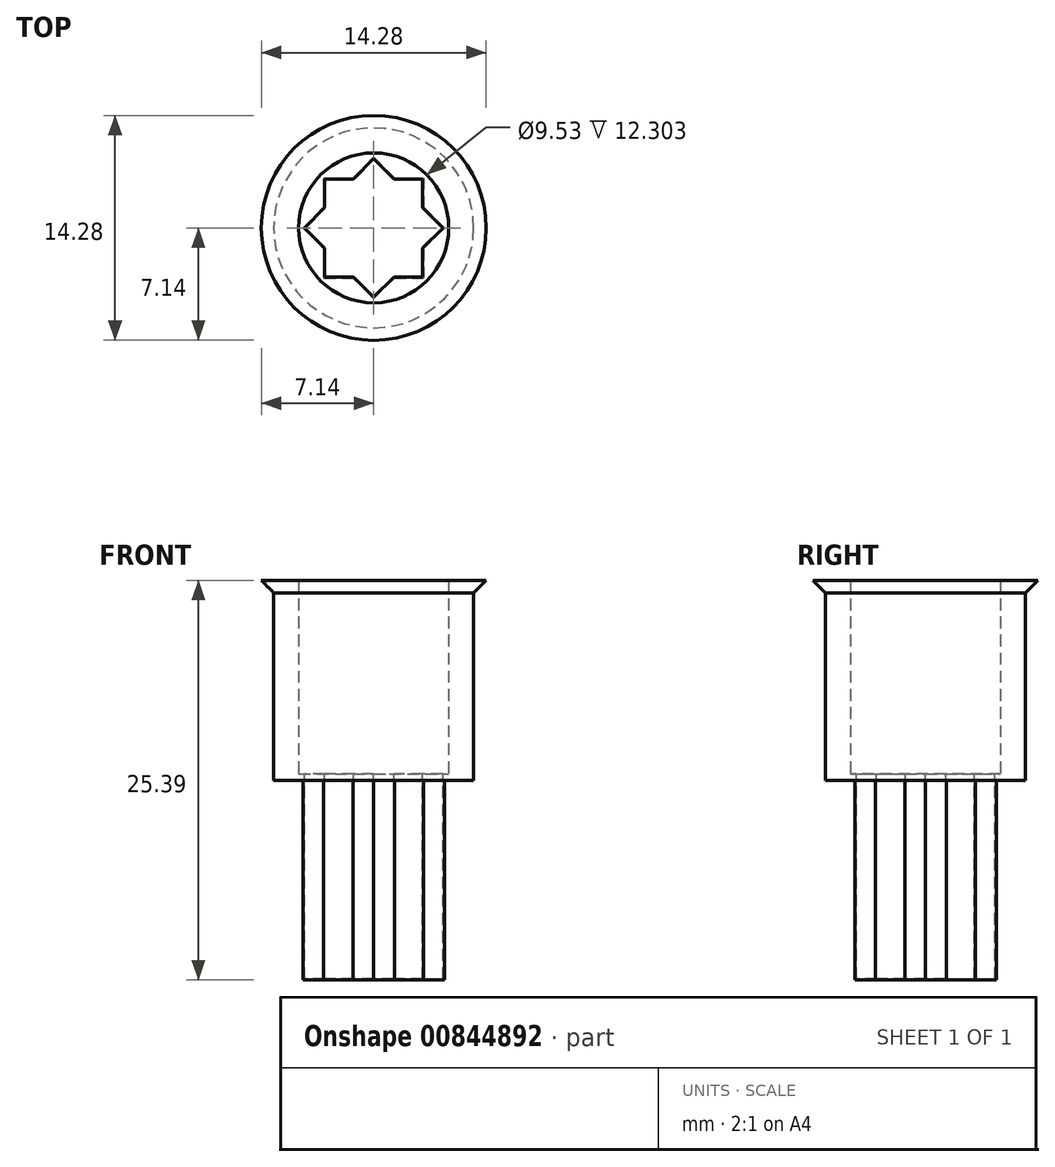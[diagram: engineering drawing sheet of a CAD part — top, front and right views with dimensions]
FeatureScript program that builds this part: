
annotation { "Feature Type Name" : "Feature", "Feature Type Description" : "" }
export const myFeature = defineFeature(function(context is Context, id is Id, definition is map)
    precondition{}
    {
        {
            var Q0;
            Q0=qCreatedBy(makeId("Top.planeOp"),FACE);
            var sketch = newSketch(context, id + "F0", { "sketchPlane" : qUnion([Q0])});
            skLineSegment(sketch, "E0.bottom", {"start": v(3.18, -3.17) * mm, "end": v(1.32, -3.18) * mm});
            skLineSegment(sketch, "E0.top", {"start": v(3.18, 3.18) * mm, "end": v(1.32, 3.18) * mm});
            skLineSegment(sketch, "E0.left", {"start": v(3.18, -3.17) * mm, "end": v(3.18, -1.32) * mm});
            skLineSegment(sketch, "E0.right", {"start": v(-3.18, -3.18) * mm, "end": v(-3.18, -1.32) * mm});
            skPoint(sketch, "E0.middle", {"position": v(0, 0) * mm});
            skLineSegment(sketch, "E1.bottom", {"start": v(3.11, -3.11) * mm, "end": v(1.29, -3.11) * mm});
            skLineSegment(sketch, "E1.top", {"start": v(3.11, 3.11) * mm, "end": v(1.29, 3.11) * mm});
            skLineSegment(sketch, "E1.left", {"start": v(3.11, -3.11) * mm, "end": v(3.11, -1.29) * mm});
            skLineSegment(sketch, "E1.right", {"start": v(-3.11, -3.11) * mm, "end": v(-3.11, -1.29) * mm});
            skLineSegment(sketch, "E2.bottom", {"start": v(0, -4.5) * mm, "end": v(-1.32, -3.17) * mm});
            skLineSegment(sketch, "E2.top", {"start": v(4.5, 0) * mm, "end": v(3.18, 1.32) * mm});
            skLineSegment(sketch, "E2.left", {"start": v(0, -4.5) * mm, "end": v(1.32, -3.17) * mm});
            skLineSegment(sketch, "E2.right", {"start": v(-4.5, 0) * mm, "end": v(-3.18, 1.32) * mm});
            skLineSegment(sketch, "E3.bottom", {"start": v(0, -4.4) * mm, "end": v(-1.29, -3.11) * mm});
            skLineSegment(sketch, "E3.top", {"start": v(4.4, 0) * mm, "end": v(3.11, 1.29) * mm});
            skLineSegment(sketch, "E3.left", {"start": v(0, -4.4) * mm, "end": v(1.29, -3.11) * mm});
            skLineSegment(sketch, "E3.right", {"start": v(-4.4, 0) * mm, "end": v(-3.11, 1.29) * mm});
            skLineSegment(sketch, "E4.trimOffspring", {"start": v(-1.29, 3.11) * mm, "end": v(0, 4.4) * mm});
            skLineSegment(sketch, "E5.trimOffspring", {"start": v(-1.32, 3.18) * mm, "end": v(0, 4.5) * mm});
            skLineSegment(sketch, "E6.trimOffspring", {"start": v(-3.11, 1.29) * mm, "end": v(-3.11, 3.11) * mm});
            skLineSegment(sketch, "E7.trimOffspring", {"start": v(-3.18, 1.32) * mm, "end": v(-3.18, 3.17) * mm});
            skLineSegment(sketch, "E8.trimOffspring", {"start": v(-1.32, 3.18) * mm, "end": v(-3.18, 3.17) * mm});
            skLineSegment(sketch, "E9.trimOffspring", {"start": v(-1.29, 3.11) * mm, "end": v(-3.11, 3.11) * mm});
            skLineSegment(sketch, "E10.trimOffspring", {"start": v(1.29, 3.11) * mm, "end": v(0, 4.4) * mm});
            skLineSegment(sketch, "E11.trimOffspring", {"start": v(1.32, 3.18) * mm, "end": v(0, 4.5) * mm});
            skLineSegment(sketch, "E12.trimOffspring", {"start": v(3.18, 1.32) * mm, "end": v(3.18, 3.18) * mm});
            skLineSegment(sketch, "E13.trimOffspring", {"start": v(3.11, 1.29) * mm, "end": v(3.11, 3.11) * mm});
            skLineSegment(sketch, "E14.trimOffspring", {"start": v(3.11, -1.29) * mm, "end": v(4.4, 0) * mm});
            skLineSegment(sketch, "E15.trimOffspring", {"start": v(3.17, -1.32) * mm, "end": v(4.5, 0) * mm});
            skLineSegment(sketch, "E16.trimOffspring", {"start": v(-1.29, -3.11) * mm, "end": v(-3.11, -3.11) * mm});
            skLineSegment(sketch, "E17.trimOffspring", {"start": v(-1.32, -3.18) * mm, "end": v(-3.18, -3.18) * mm});
            skLineSegment(sketch, "E18.trimOffspring", {"start": v(-3.11, -1.29) * mm, "end": v(-4.4, 0) * mm});
            skLineSegment(sketch, "E19.trimOffspring", {"start": v(-3.18, -1.32) * mm, "end": v(-4.5, 0) * mm});
            skSolve(sketch);
        }
        {
            var Q0;
            Q0 = qSketchRegion(id + "F0", true);
            extrude(context, id + "F1", {"entities" : qUnion([Q0]), "oppositeDirection" : true, "depth" : 12.7 * mm, "offsetDistance" : 25.4 * mm});
        }
        {
            var Q0;
            Q0=qCreatedBy(makeId("Front.planeOp"),FACE);
            var sketch = newSketch(context, id + "F2", { "sketchPlane" : qUnion([Q0])});
            skLineSegment(sketch, "E20", {"start": v(0, 0) * mm, "end": v(0, 0.4) * mm});
            skLineSegment(sketch, "E21", {"start": v(-4.76, 12.7) * mm, "end": v(-7.14, 12.7) * mm});
            skLineSegment(sketch, "E22", {"start": v(-7.14, 0) * mm, "end": v(0, 0) * mm});
            skLineSegment(sketch, "E23", {"start": v(0, 0.4) * mm, "end": v(-4.76, 0.4) * mm});
            skLineSegment(sketch, "E24", {"start": v(-4.76, 0.4) * mm, "end": v(-4.76, 12.7) * mm});
            skLineSegment(sketch, "E25", {"start": v(-6.35, 0) * mm, "end": v(-6.35, 12.7) * mm});
            skLineSegment(sketch, "E26", {"start": v(-7.14, 12.7) * mm, "end": v(-6.35, 11.9) * mm});
            skSolve(sketch);
        }
        {
            var Q0;
            Q0 = qSketchRegion(id + "F2", true);
            var Q1;
            Q1=sQuery(id+"F2.wireOp",EDGE,"E20");
            revolve(context, id + "F3", {"operationType" : NewBodyOperationType.ADD, "surfaceOperationType" : NewSurfaceOperationType.NEW, "entities" : qUnion([Q0]), "axis" : qUnion([Q1]), "revolveType" : RevolveType.FULL});
        }
        {
            var Q0;
            Q0=makeQuery(id+"F3.boolean.opBoolean","SPLIT",FACE,{"disambiguationData":[TD([makeQuery(id+"F1.opExtrude","SWEPT_FACE",FACE,{"disambiguationData":[OSD([sQuery(id+"F0.wireOp",EDGE,"E1.bottom")])]})])],"derivedFrom":makeQuery(id+"F3.opRevolve","SWEPT_FACE",FACE,{"disambiguationData":[OSD([sQuery(id+"F2.wireOp",EDGE,"E22")])]})});
            extrude(context, id + "F4", {"entities" : qUnion([Q0]), "operationType" : NewBodyOperationType.REMOVE, "oppositeDirection" : true, "depth" : 25.4 * mm, "offsetDistance" : 25.4 * mm});
        }
        {
            var Q0;
            Q0=makeQuery(id+"F1.opExtrude","CAP_EDGE",EDGE,{"disambiguationData":[OSD([sQuery(id+"F0.wireOp",EDGE,"E3.left")])],"isStart":false});
            var Q1;
            Q1=makeQuery(id+"F1.opExtrude","CAP_EDGE",EDGE,{"disambiguationData":[OSD([sQuery(id+"F0.wireOp",EDGE,"E1.bottom")])],"isStart":false});
            var Q2;
            Q2=makeQuery(id+"F1.opExtrude","CAP_EDGE",EDGE,{"disambiguationData":[OSD([sQuery(id+"F0.wireOp",EDGE,"E1.left")])],"isStart":false});
            var Q3;
            Q3=makeQuery(id+"F1.opExtrude","CAP_EDGE",EDGE,{"disambiguationData":[OSD([sQuery(id+"F0.wireOp",EDGE,"E14.trimOffspring")])],"isStart":false});
            var Q4;
            Q4=makeQuery(id+"F1.opExtrude","CAP_EDGE",EDGE,{"disambiguationData":[OSD([sQuery(id+"F0.wireOp",EDGE,"E3.top")])],"isStart":false});
            var Q5;
            Q5=makeQuery(id+"F1.opExtrude","CAP_EDGE",EDGE,{"disambiguationData":[OSD([sQuery(id+"F0.wireOp",EDGE,"E13.trimOffspring")])],"isStart":false});
            var Q6;
            Q6=makeQuery(id+"F1.opExtrude","CAP_EDGE",EDGE,{"disambiguationData":[OSD([sQuery(id+"F0.wireOp",EDGE,"E1.top")])],"isStart":false});
            var Q7;
            Q7=makeQuery(id+"F1.opExtrude","CAP_EDGE",EDGE,{"disambiguationData":[OSD([sQuery(id+"F0.wireOp",EDGE,"E10.trimOffspring")])],"isStart":false});
            var Q8;
            Q8=makeQuery(id+"F1.opExtrude","CAP_EDGE",EDGE,{"disambiguationData":[OSD([sQuery(id+"F0.wireOp",EDGE,"E4.trimOffspring")])],"isStart":false});
            var Q9;
            Q9=makeQuery(id+"F1.opExtrude","CAP_EDGE",EDGE,{"disambiguationData":[OSD([sQuery(id+"F0.wireOp",EDGE,"E9.trimOffspring")])],"isStart":false});
            var Q10;
            Q10=makeQuery(id+"F1.opExtrude","CAP_EDGE",EDGE,{"disambiguationData":[OSD([sQuery(id+"F0.wireOp",EDGE,"E6.trimOffspring")])],"isStart":false});
            var Q11;
            Q11=makeQuery(id+"F1.opExtrude","CAP_EDGE",EDGE,{"disambiguationData":[OSD([sQuery(id+"F0.wireOp",EDGE,"E3.right")])],"isStart":false});
            var Q12;
            Q12=makeQuery(id+"F1.opExtrude","CAP_EDGE",EDGE,{"disambiguationData":[OSD([sQuery(id+"F0.wireOp",EDGE,"E18.trimOffspring")])],"isStart":false});
            var Q13;
            Q13=makeQuery(id+"F1.opExtrude","CAP_EDGE",EDGE,{"disambiguationData":[OSD([sQuery(id+"F0.wireOp",EDGE,"E1.right")])],"isStart":false});
            var Q14;
            Q14=makeQuery(id+"F1.opExtrude","CAP_EDGE",EDGE,{"disambiguationData":[OSD([sQuery(id+"F0.wireOp",EDGE,"E16.trimOffspring")])],"isStart":false});
            var Q15;
            Q15=makeQuery(id+"F1.opExtrude","CAP_EDGE",EDGE,{"disambiguationData":[OSD([sQuery(id+"F0.wireOp",EDGE,"E3.bottom")])],"isStart":false});
            chamfer(context, id + "F5", {"entities" : qUnion([Q0, Q1, Q2, Q3, Q4, Q5, Q6, Q7, Q8, Q9, Q10, Q11, Q12, Q13, Q14, Q15]), "width" : 0.08 * mm, "tangentPropagation" : true});
        }
    });
